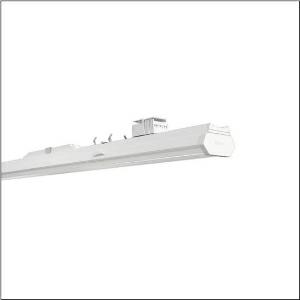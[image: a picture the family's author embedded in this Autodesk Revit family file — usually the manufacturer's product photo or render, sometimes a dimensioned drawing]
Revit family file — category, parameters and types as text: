
# Revit family: licross_r__21_protected_mo_52td11dn4a5g_03df
name_source: partatom
category: Lighting Fixtures
units: mm (PartAtom-declared; Revit-internal decimal feet)

## family parameters
Cut with Voids When Loaded = No
Host = Face
Light Source = No
Part Type = Normal
Room Calculation Point = No
Round Connector Dimension = Use Diameter
Shared = No

## types (1)
- --- (1 x LED, 10650 lm, 62 W, 4000K)
    Apparent Load = 62 VA
    CIE Flux Codes = 83 94 98 100 100
    Color Rendering = 80
    Color Temperature = 4000K
    Default Elevation = 1800 mm
    Description = Licross® 21 Protected MO, luminaire insert, of sheet steel, galvanised, coil coated, white, length: 1.500mm, width: 90mm, height: 103mm, LED rated luminous flux: 10.650lm, light colour: 840, control gear: DALI 2, with plug, 5-pole, with phase selection, mains connection: 220..240V, AC, 50/60Hz, rated input power: 62W, halogen-free wiring, primary light control with lens, of plastic, primary optical cover: cover, of PMMA, light emission: direct distribution, primary light characteristic: symmetric, protection rating (complete): IP54, insulation class (complete): insulation class I (protective earthing), certification: CE, ENEC, VDE, UKCA, protection symbol: D if used in an environment with non-conductive dust loads with corresponding accessories, impact resistance: IK06, permissible ambient temperature for indoor applications: -25..+35°C, corresponds to IFS (International Featured Standards) requirements for safety and quality in the food industry, reducing of maximum allowable ambient temperature of 5°C with ceiling mounting, LABS conformity tested according to VDMA 24364:2018-05, packaging unit: 1 piece
    Height = 92 mm
    Lamp = 1 x LED
    Lamp Light Flux = 10650 lm
    Lamp Power = 62 W
    Lamp count = 1
    Length = 1500 mm
    Luminous efficacy = 172 lm/W
    Manufacturer = Siteco
    ModVariant = No
    Model = 52TD11DN4A5G
    Mounting Place = Ceiling
    Mounting Type = Pendant
    Number of Poles = 1
    OnlyDefault = Yes
    Power Factor = 1
    Product Name = Licross® 21 Protected MO
    Product group = luminaire insert
    ProductGroupID = 902
    Protection Class = Protection class I
    Protection Degree = IP 54
    RLX_Detail_Level = 1
    RLX_Emergency_Light_Flux = 0 lm
    RLX_Emergency_Type = 0
    RLX_Emergency_Type_DB = No
    RlxData = <blob elided: 24157 chars, md5=7bea5dc8>
    Socket = socket
    Standby Power = 0 W
    System Light Flux = 10650 lm
    System Power = 62 W
    Type Comments = factory setting: luminous flux: 100 % | dim-lin: 254 | 418 mA
    Type Image = l_1256148.jpg
    URL = http://relux.com
    VarID = @adj_128300
    Voltage = 0 V
    Weight = 0.00 kg
    Width = 88 mm

## geometry (parser evidence)
native form markers: Blend x4, Sweep x11
no freeform markers — native parametric forms only
